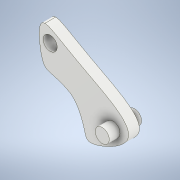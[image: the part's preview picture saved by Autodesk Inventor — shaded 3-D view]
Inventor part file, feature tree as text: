
AUTODESK INVENTOR PART (.ipt)
format: ipt  version: 2022 (Build 260153000, 153)  size: 134,144 bytes
history: native  units: in
note: dims shown in document units (in); Inventor stores cm internally (conversion verified against a paired STEP export)
features: extrude x3, sketch x2, projected_geometry x1
ambient origin geometry x8: Origin, YZ Plane, XZ Plane, XY Plane, X Axis, Y Axis, Z Axis, Center Point
bodies: Solid1 (feature_tree)
feature tree (6):
  sketch  "Sketch2"  dims[d0=0.1969in d1=0.0in d2=0.1969in d3=0.0in]
  extrude  "Extrusion1"  Depth=0.1969in TaperAngle=0.0deg
  extrude  "Extrusion2"  Depth=0.2559in
  extrude  "Extrusion3"  [1 undecoded]
  sketch  "Sketch3"  dims[d4=0.1969in d5=0.0in d6=0.2559in]
  projected_geometry  "Projected Loop2"
note: 1 required parameter value undecoded (feature->parameter linkage not recoverable at this tier; creation-order binding heuristic only, values carry confidence <= 0.55)
